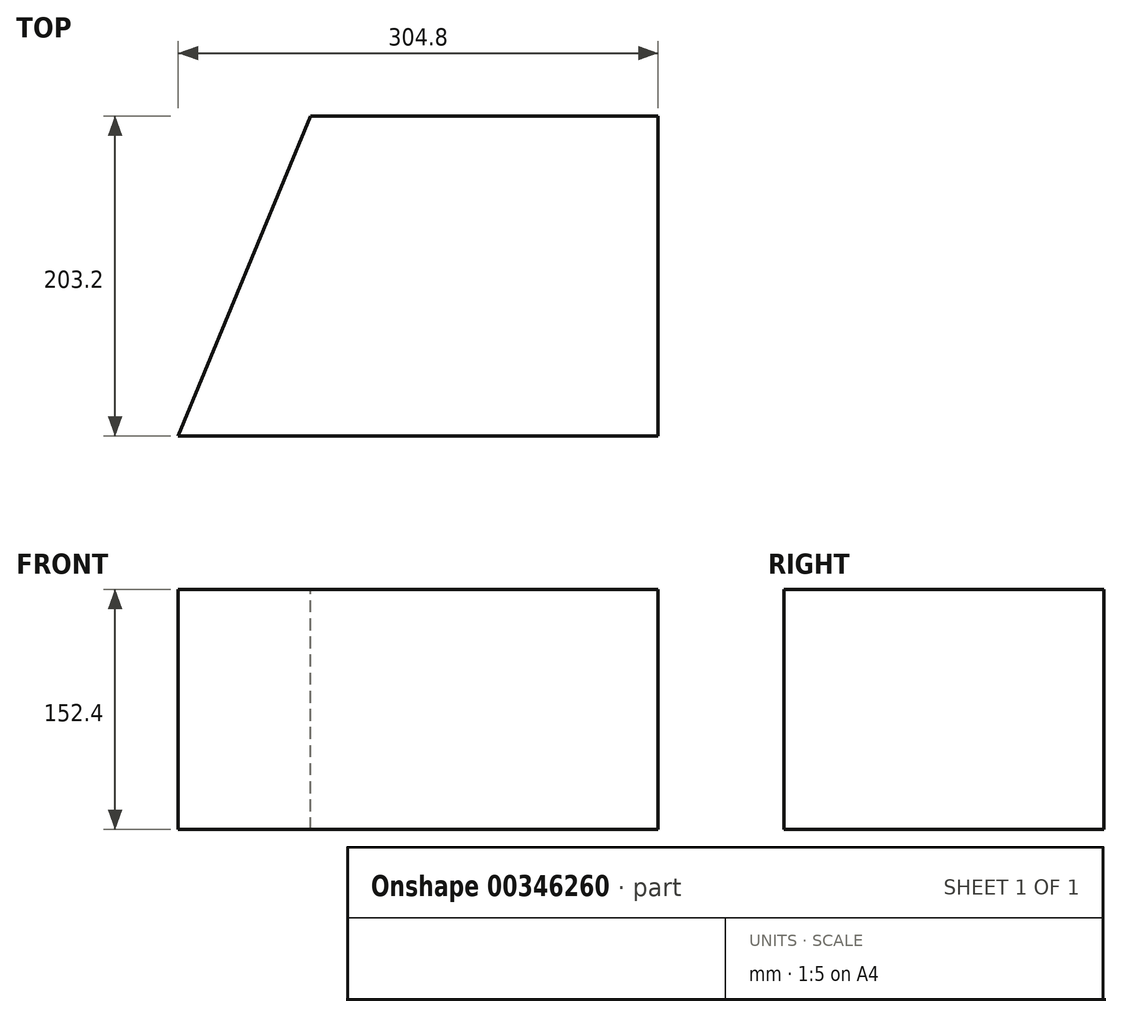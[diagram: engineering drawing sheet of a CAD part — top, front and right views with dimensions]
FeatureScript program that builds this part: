
annotation { "Feature Type Name" : "Feature", "Feature Type Description" : "" }
export const myFeature = defineFeature(function(context is Context, id is Id, definition is map)
    precondition{}
    {
        {
            var Q0;
            Q0=qCreatedBy(makeId("Right.planeOp"),FACE);
            var sketch = newSketch(context, id + "F0", { "sketchPlane" : qUnion([Q0])});
            skLineSegment(sketch, "E0.bottom", {"start": v(-101.6, 76.2) * mm, "end": v(101.6, 76.2) * mm});
            skLineSegment(sketch, "E0.top", {"start": v(-101.6, -76.2) * mm, "end": v(101.6, -76.2) * mm});
            skLineSegment(sketch, "E0.left", {"start": v(-101.6, 76.2) * mm, "end": v(-101.6, -76.2) * mm});
            skLineSegment(sketch, "E0.right", {"start": v(101.6, 76.2) * mm, "end": v(101.6, -76.2) * mm});
            skSolve(sketch);
        }
        {
            var Q0;
            Q0=makeQuery(id+"F0.imprint","IMPRINT",FACE,{"disambiguationData":[TD([[makeQuery(id+"F0.imprint","IMPRINT",EDGE,{"derivedFrom":sQuery(id+"F0.wireOp",EDGE,"E0.bottom")}),-1.0]])]});
            extrude(context, id + "F1", {"entities" : qUnion([Q0]), "endBound" : BoundingType.SYMMETRIC, "depth" : 304.8 * mm});
        }
        {
            var Q0;
            Q0=makeQuery(id+"F1.opExtrude","SWEPT_FACE",FACE,{"disambiguationData":[OSD([sQuery(id+"F0.wireOp",EDGE,"E0.bottom")])]});
            var sketch = newSketch(context, id + "F2", { "sketchPlane" : qUnion([Q0])});
            skLineSegment(sketch, "E1", {"start": v(-152.4, -101.6) * mm, "end": v(-68.23, 101.6) * mm});
            skLineSegment(sketch, "E2", {"start": v(-68.23, 101.6) * mm, "end": v(-152.4, 101.6) * mm});
            skLineSegment(sketch, "E3", {"start": v(-152.4, 101.6) * mm, "end": v(-152.4, -101.6) * mm});
            skSolve(sketch);
        }
        {
            var Q0;
            Q0=qSketchRegion(id+"F2",true);
            extrude(context, id + "F3", {"entities" : qUnion([Q0]), "operationType" : NewBodyOperationType.REMOVE, "endBound" : BoundingType.THROUGH_ALL, "oppositeDirection" : true, "depth" : 25.4 * mm});
        }
    });
